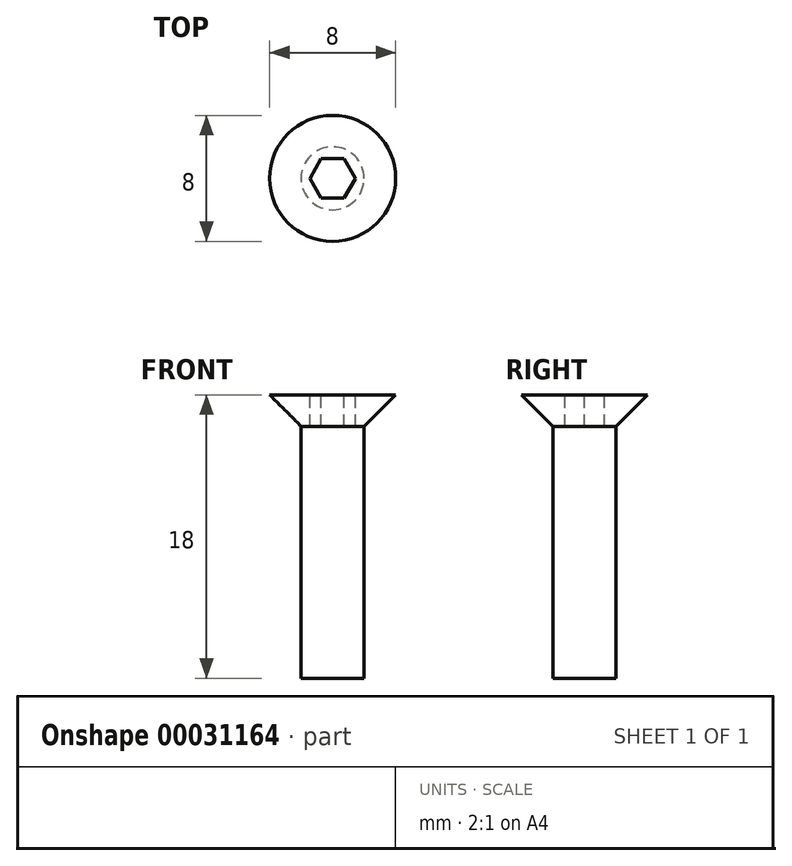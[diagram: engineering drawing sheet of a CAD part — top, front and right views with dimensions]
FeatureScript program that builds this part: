
annotation { "Feature Type Name" : "Feature", "Feature Type Description" : "" }
export const myFeature = defineFeature(function(context is Context, id is Id, definition is map)
    precondition{}
    {
        {
            var Q0;
            Q0=qCreatedBy(makeId("Front.planeOp"),FACE);
            var sketch = newSketch(context, id + "F0", { "sketchPlane" : qUnion([Q0])});
            skLineSegment(sketch, "E0", {"start": v(0, 0) * mm, "end": v(4, 0) * mm});
            skLineSegment(sketch, "E1", {"start": v(4, 0) * mm, "end": v(2, -2) * mm});
            skLineSegment(sketch, "E2", {"start": v(2, -2) * mm, "end": v(2, -18) * mm});
            skLineSegment(sketch, "E3", {"start": v(2, -18) * mm, "end": v(0, -18) * mm});
            skLineSegment(sketch, "E4", {"start": v(0, -18) * mm, "end": v(0, 0) * mm});
            skSolve(sketch);
        }
        {
            var Q0;
            Q0=makeQuery(id+"F0.imprint","IMPRINT",FACE,{"disambiguationData":[TD([[makeQuery(id+"F0.imprint","IMPRINT",EDGE,{"derivedFrom":sQuery(id+"F0.wireOp",EDGE,"E0")}),-1.0]])]});
            var Q1;
            Q1=sQuery(id+"F0.wireOp",EDGE,"E4");
            revolve(context, id + "F1", {"entities" : qUnion([Q0]), "axis" : qUnion([Q1]), "revolveType" : RevolveType.FULL});
        }
        {
            var Q0;
            Q0=makeQuery(id+"F1.opRevolve","SWEPT_FACE",FACE,{"disambiguationData":[OSD([sQuery(id+"F0.wireOp",EDGE,"E0")])]});
            var sketch = newSketch(context, id + "F2", { "sketchPlane" : qUnion([Q0])});
            skCircle(sketch, "E5.cCircle", {"center": v(0, 0) * mm, "radius": 1.25 * mm, "construction": true});
            skLineSegment(sketch, "E5.0", {"start": v(-0.72, 1.25) * mm, "end": v(0.72, 1.25) * mm});
            skLineSegment(sketch, "E5.1", {"start": v(0.72, 1.25) * mm, "end": v(1.44, 0) * mm});
            skLineSegment(sketch, "E5.2", {"start": v(1.44, 0) * mm, "end": v(0.72, -1.25) * mm});
            skLineSegment(sketch, "E5.3", {"start": v(0.72, -1.25) * mm, "end": v(-0.72, -1.25) * mm});
            skLineSegment(sketch, "E5.4", {"start": v(-0.72, -1.25) * mm, "end": v(-1.44, 0) * mm});
            skLineSegment(sketch, "E5.5", {"start": v(-1.44, 0) * mm, "end": v(-0.72, 1.25) * mm});
            skPoint(sketch, "E5.0.midPoint", {"position": v(0, 1.25) * mm});
            skSolve(sketch);
        }
        {
            var Q0;
            Q0 = qSketchRegion(id + "F2", true);
            extrude(context, id + "F3", {"entities" : qUnion([Q0]), "operationType" : NewBodyOperationType.REMOVE, "oppositeDirection" : true, "depth" : 2 * mm});
        }
    });
